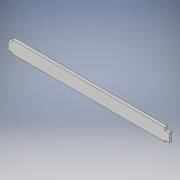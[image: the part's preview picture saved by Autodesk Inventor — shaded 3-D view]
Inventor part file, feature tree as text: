
AUTODESK INVENTOR PART (.ipt)
format: ipt  version: 2018 (Build 220112000, 112)  size: 106,496 bytes
history: native  units: in
note: dims shown in document units (in); Inventor stores cm internally (conversion verified against a paired STEP export)
features: extrude x1, sketch x1
ambient origin geometry x8: Origin, YZ Plane, XZ Plane, XY Plane, X Axis, Y Axis, Z Axis, Center Point
bodies: Solid1 (feature_tree)
feature tree (2):
  extrude  "Extrusion1"  Depth=0.45in
  sketch  "Sketch1"  dims[d0=5.5in d1=0.45in d2=0.15in d3=0.3in d4=0.05in d5=0.15in d6=0.3in d7=0.05in d8=0.1in d9=0.0in]
